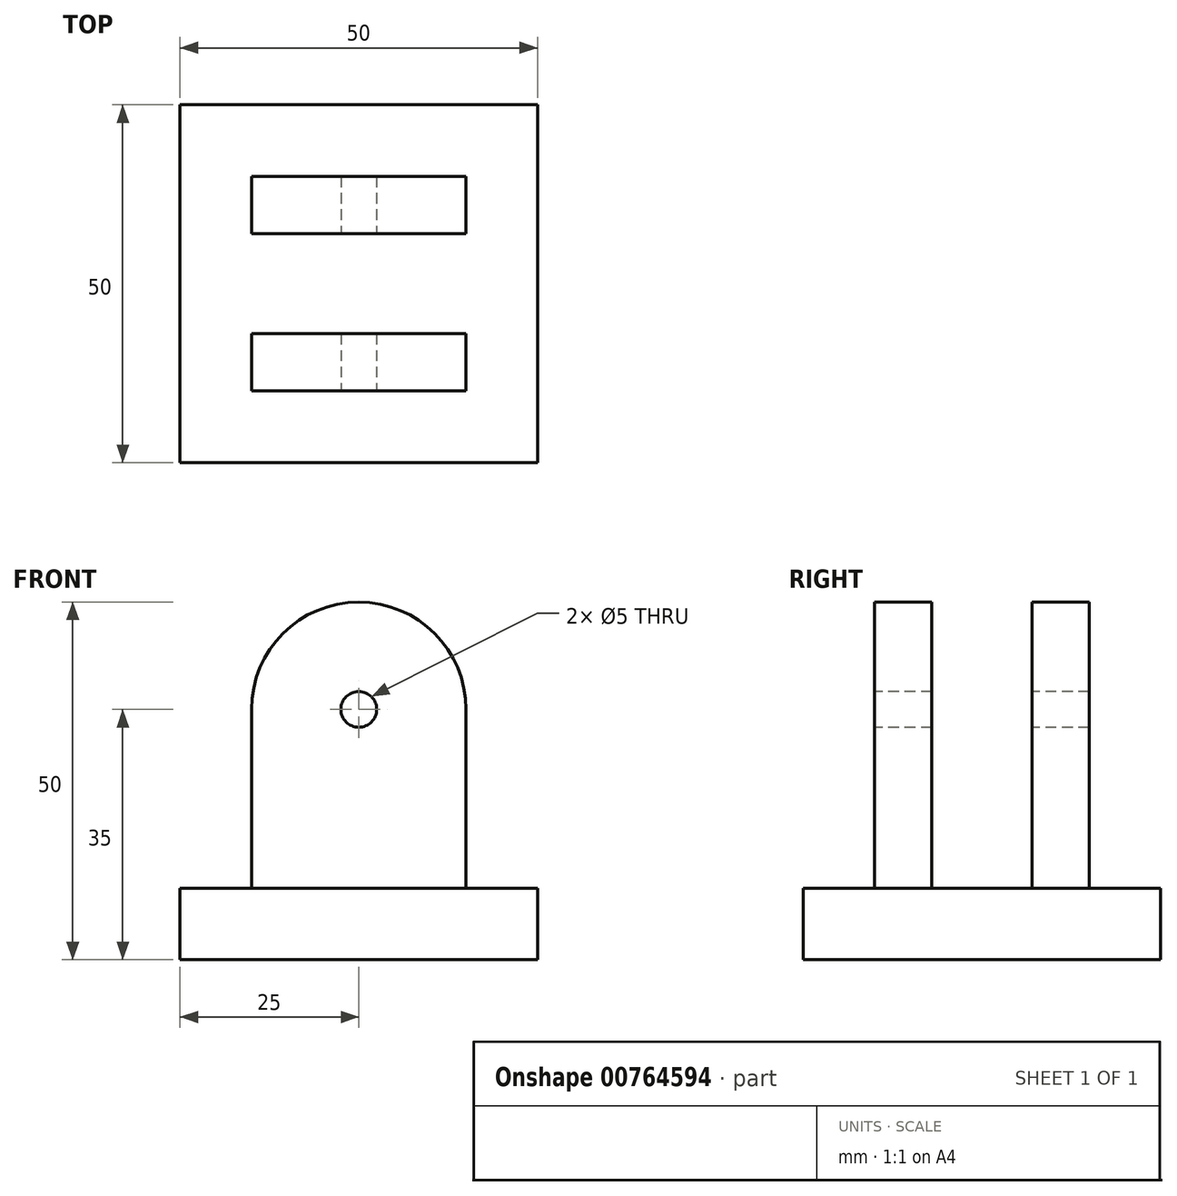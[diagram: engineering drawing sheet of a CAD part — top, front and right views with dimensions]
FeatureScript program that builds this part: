
annotation { "Feature Type Name" : "Feature", "Feature Type Description" : "" }
export const myFeature = defineFeature(function(context is Context, id is Id, definition is map)
    precondition{}
    {
        {
            var Q0;
            Q0=qCreatedBy(makeId("Top.planeOp"),FACE);
            var sketch = newSketch(context, id + "F0", { "sketchPlane" : qUnion([Q0])});
            skLineSegment(sketch, "E0.bottom", {"start": v(25, 25) * mm, "end": v(-25, 25) * mm});
            skLineSegment(sketch, "E0.top", {"start": v(25, -25) * mm, "end": v(-25, -25) * mm});
            skLineSegment(sketch, "E0.left", {"start": v(25, 25) * mm, "end": v(25, -25) * mm});
            skLineSegment(sketch, "E0.right", {"start": v(-25, 25) * mm, "end": v(-25, -25) * mm});
            skPoint(sketch, "E0.middle", {"position": v(0, 0) * mm});
            skSolve(sketch);
        }
        {
            var Q0;
            Q0=makeQuery(id+"F0.imprint","IMPRINT",FACE,{"disambiguationData":[TD([[makeQuery(id+"F0.imprint","IMPRINT",EDGE,{"derivedFrom":sQuery(id+"F0.wireOp",EDGE,"E0.bottom")}),1.0]])]});
            extrude(context, id + "F1", {"entities" : qUnion([Q0]), "depth" : 10 * mm, "offsetDistance" : 25 * mm});
        }
        {
            var Q0;
            Q0=qCreatedBy(makeId("Top.planeOp"),FACE);
            var sketch = newSketch(context, id + "F2", { "sketchPlane" : qUnion([Q0])});
            skLineSegment(sketch, "E1.bottom", {"start": v(-15, 15) * mm, "end": v(15, 15) * mm});
            skLineSegment(sketch, "E1.top", {"start": v(-15, 7) * mm, "end": v(15, 7) * mm});
            skLineSegment(sketch, "E1.left", {"start": v(-15, 15) * mm, "end": v(-15, 7) * mm});
            skLineSegment(sketch, "E1.right", {"start": v(15, 15) * mm, "end": v(15, 7) * mm});
            skLineSegment(sketch, "E2.bottom", {"start": v(-15, -7) * mm, "end": v(15, -7) * mm});
            skLineSegment(sketch, "E2.top", {"start": v(-15, -15) * mm, "end": v(15, -15) * mm});
            skLineSegment(sketch, "E2.left", {"start": v(-15, -7) * mm, "end": v(-15, -15) * mm});
            skLineSegment(sketch, "E2.right", {"start": v(15, -7) * mm, "end": v(15, -15) * mm});
            skSolve(sketch);
        }
        {
            var Q0;
            Q0=makeQuery(id+"F2.imprint","IMPRINT",FACE,{"disambiguationData":[TD([[makeQuery(id+"F2.imprint","IMPRINT",EDGE,{"derivedFrom":sQuery(id+"F2.wireOp",EDGE,"E1.bottom")}),-1.0]])]});
            var Q1;
            Q1=makeQuery(id+"F2.imprint","IMPRINT",FACE,{"disambiguationData":[TD([[makeQuery(id+"F2.imprint","IMPRINT",EDGE,{"derivedFrom":sQuery(id+"F2.wireOp",EDGE,"E2.bottom")}),-1.0]])]});
            extrude(context, id + "F3", {"entities" : qUnion([Q0, Q1]), "operationType" : NewBodyOperationType.ADD, "depth" : 50 * mm, "offsetDistance" : 25 * mm});
        }
        {
            var Q0;
            Q0=makeQuery(id+"F3.opExtrude","CAP_EDGE",EDGE,{"disambiguationData":[OSD([sQuery(id+"F2.wireOp",EDGE,"E2.left")])],"isStart":false});
            var Q1;
            Q1=makeQuery(id+"F3.opExtrude","CAP_EDGE",EDGE,{"disambiguationData":[OSD([sQuery(id+"F2.wireOp",EDGE,"E1.left")])],"isStart":false});
            var Q2;
            Q2=makeQuery(id+"F3.opExtrude","CAP_EDGE",EDGE,{"disambiguationData":[OSD([sQuery(id+"F2.wireOp",EDGE,"E1.right")])],"isStart":false});
            var Q3;
            Q3=makeQuery(id+"F3.opExtrude","CAP_EDGE",EDGE,{"disambiguationData":[OSD([sQuery(id+"F2.wireOp",EDGE,"E2.right")])],"isStart":false});
            fillet(context, id + "F4", {"entities" : qUnion([Q0, Q1, Q2, Q3]), "radius" : 15 * mm, "tangentPropagation" : true, "allowEdgeOverflow" : false});
        }
        {
            var Q0;
            Q0=makeQuery(id+"F3.opExtrude","SWEPT_FACE",FACE,{"disambiguationData":[OSD([sQuery(id+"F2.wireOp",EDGE,"E2.top")])]});
            var sketch = newSketch(context, id + "F5", { "sketchPlane" : qUnion([Q0])});
            skPoint(sketch, "E3", {"position": v(0, 35) * mm});
            skSolve(sketch);
        }
        {
            var Q0;
            Q0=sQuery(id+"F5.wireOp",VERTEX,"E3");
            var Q1;
            Q1=makeQuery(id+"F1.opExtrude","SWEPT_BODY",BODY,{"disambiguationData":[OSD([sQuery(id+"F0.wireOp",EDGE,"E0.bottom"),sQuery(id+"F0.wireOp",EDGE,"E0.top"),sQuery(id+"F0.wireOp",EDGE,"E0.left"),sQuery(id+"F0.wireOp",EDGE,"E0.right")])]});
            hole(context, id + "F6", {"style" : HoleStyle.SIMPLE, "endStyle" : HoleEndStyle.THROUGH, "holeDiameter" : 5 * mm, "majorDiameter" : 5 * mm, "isTappedThrough" : true, "tappedDepth" : 12 * mm, "tapClearance" : 3, "locations" : qUnion([Q0]), "scope" : qUnion([Q1])});
        }
    });
